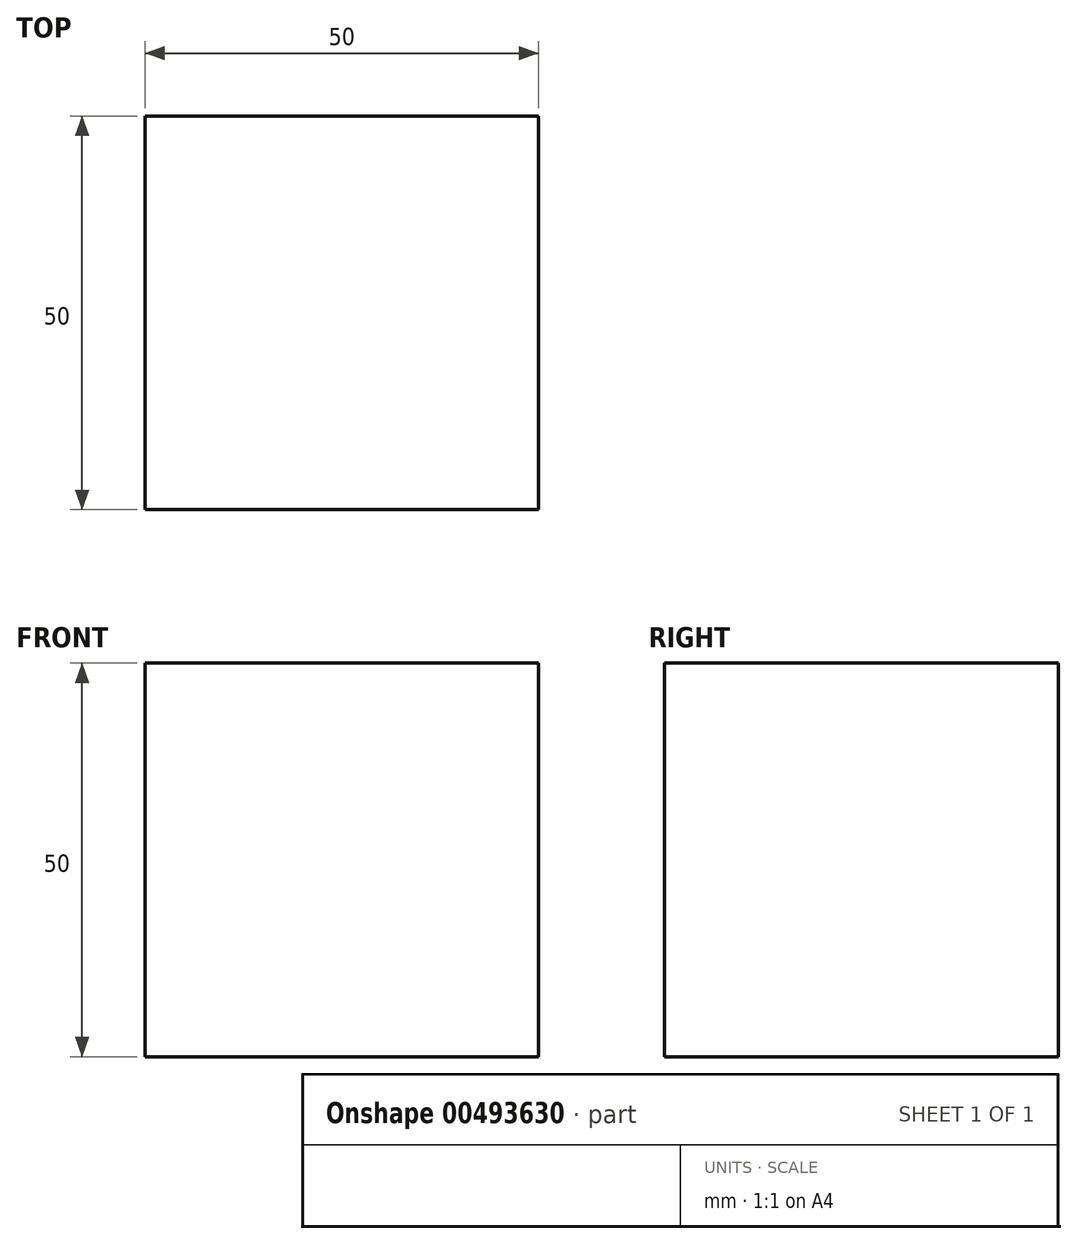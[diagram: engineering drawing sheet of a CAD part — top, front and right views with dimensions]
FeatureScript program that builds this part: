
annotation { "Feature Type Name" : "Feature", "Feature Type Description" : "" }
export const myFeature = defineFeature(function(context is Context, id is Id, definition is map)
    precondition{}
    {
        {
            var Q0;
            Q0=qCreatedBy(makeId("Front.planeOp"),FACE);
            var sketch = newSketch(context, id + "F0", { "sketchPlane" : qUnion([Q0])});
            skLineSegment(sketch, "E0.bottom", {"start": v(25, 25) * mm, "end": v(-25, 25) * mm});
            skLineSegment(sketch, "E0.top", {"start": v(25, -25) * mm, "end": v(-25, -25) * mm});
            skLineSegment(sketch, "E0.left", {"start": v(25, 25) * mm, "end": v(25, -25) * mm});
            skLineSegment(sketch, "E0.right", {"start": v(-25, 25) * mm, "end": v(-25, -25) * mm});
            skPoint(sketch, "E0.middle", {"position": v(0, 0) * mm});
            skSolve(sketch);
        }
        {
            var Q0;
            Q0=makeQuery(id+"F0.imprint","IMPRINT",FACE,{"disambiguationData":[TD([[makeQuery(id+"F0.imprint","IMPRINT",EDGE,{"derivedFrom":sQuery(id+"F0.wireOp",EDGE,"E0.bottom")}),1.0]])]});
            extrude(context, id + "F1", {"entities" : qUnion([Q0]), "depth" : 50 * mm});
        }
    });
